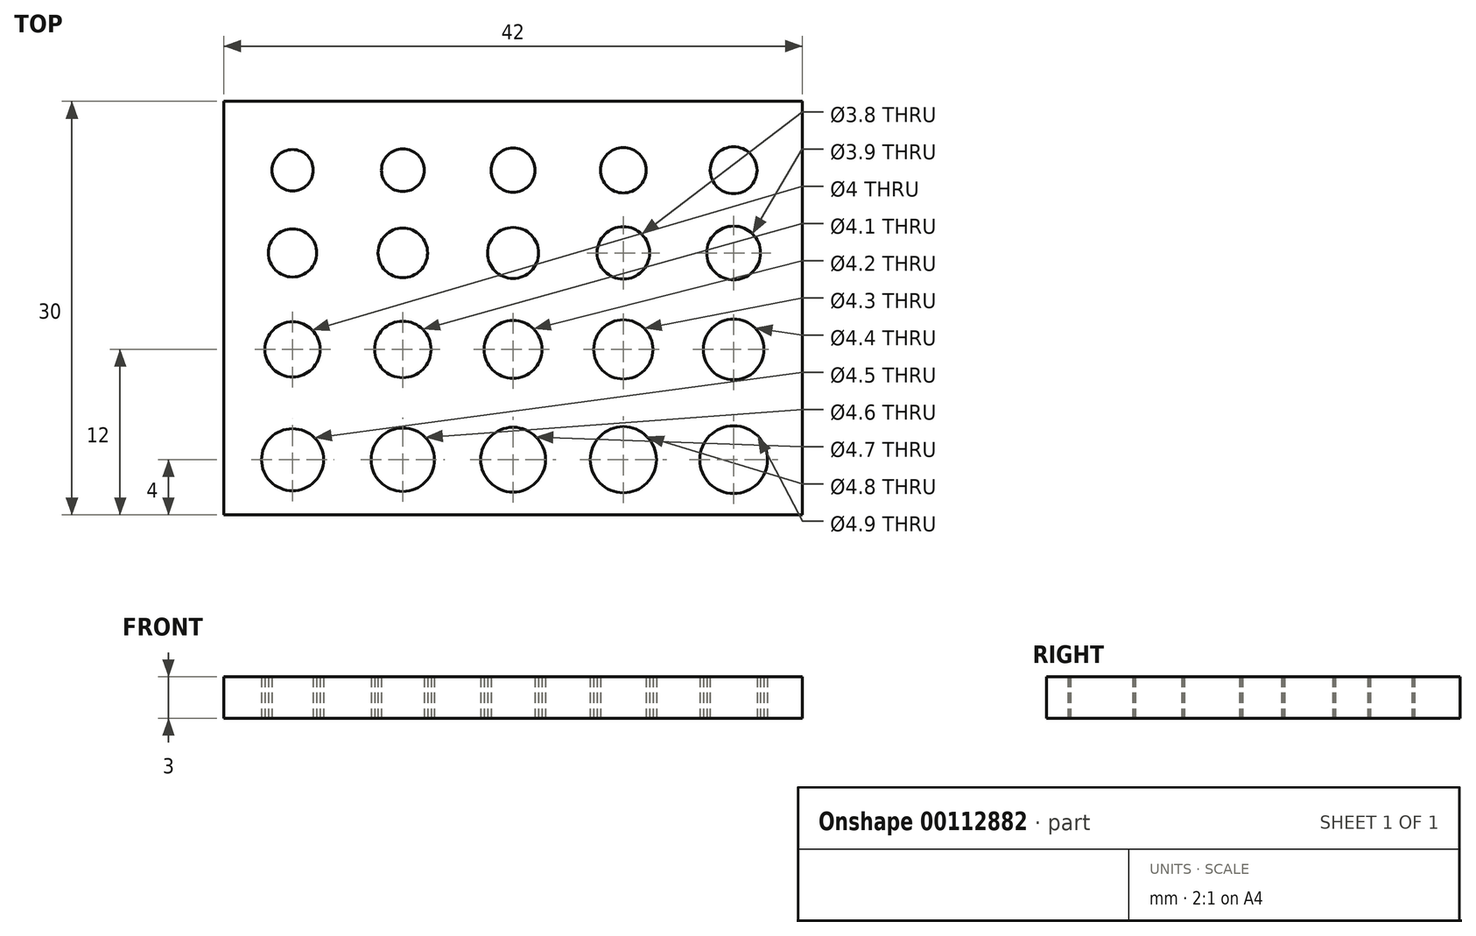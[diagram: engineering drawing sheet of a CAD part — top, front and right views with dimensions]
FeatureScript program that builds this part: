
annotation { "Feature Type Name" : "Feature", "Feature Type Description" : "" }
export const myFeature = defineFeature(function(context is Context, id is Id, definition is map)
    precondition{}
    {
        {
            var Q0;
            Q0=qCreatedBy(makeId("Top.planeOp"),FACE);
            var sketch = newSketch(context, id + "F0", { "sketchPlane" : qUnion([Q0])});
            skLineSegment(sketch, "E0.bottom", {"start": v(21, 15) * mm, "end": v(-21, 15) * mm});
            skLineSegment(sketch, "E0.top", {"start": v(21, -15) * mm, "end": v(-21, -15) * mm});
            skLineSegment(sketch, "E0.left", {"start": v(21, 15) * mm, "end": v(21, -15) * mm});
            skLineSegment(sketch, "E0.right", {"start": v(-21, 15) * mm, "end": v(-21, -15) * mm});
            skPoint(sketch, "E0.middle", {"position": v(0, 0) * mm});
            skPoint(sketch, "E1", {"position": v(-16, 10) * mm});
            skPoint(sketch, "E2.1.0.0", {"position": v(-8, 10) * mm});
            skPoint(sketch, "E2.2.0.0", {"position": v(0, 10) * mm});
            skLineSegment(sketch, "E2.direction1", {"start": v(-16, 10) * mm, "end": v(-8, 10) * mm, "construction": true});
            skPoint(sketch, "E3.0.3.0", {"position": v(8, 10) * mm});
            skPoint(sketch, "E3.0.4.0", {"position": v(16, 10) * mm});
            skPoint(sketch, "E4", {"position": v(-16, 4) * mm});
            skPoint(sketch, "E5", {"position": v(-16, -3) * mm});
            skPoint(sketch, "E6", {"position": v(-16, -11) * mm});
            skPoint(sketch, "E7.1.0.0", {"position": v(-8, 4) * mm});
            skPoint(sketch, "E7.2.0.0", {"position": v(0, 4) * mm});
            skLineSegment(sketch, "E7.direction1", {"start": v(-16, 4) * mm, "end": v(-8, 4) * mm, "construction": true});
            skPoint(sketch, "E8.0.3.0", {"position": v(8, 4) * mm});
            skPoint(sketch, "E8.0.4.0", {"position": v(16, 4) * mm});
            skPoint(sketch, "E9.1.0.0", {"position": v(-8, -3) * mm});
            skPoint(sketch, "E9.2.0.0", {"position": v(0, -3) * mm});
            skLineSegment(sketch, "E9.direction1", {"start": v(-16, -3) * mm, "end": v(-8, -3) * mm, "construction": true});
            skPoint(sketch, "E10.0.3.0", {"position": v(8, -3) * mm});
            skPoint(sketch, "E10.0.4.0", {"position": v(16, -3) * mm});
            skPoint(sketch, "E11.1.0.0", {"position": v(-8, -11) * mm});
            skPoint(sketch, "E11.2.0.0", {"position": v(0, -11) * mm});
            skLineSegment(sketch, "E11.direction1", {"start": v(-16, -11) * mm, "end": v(-8, -11) * mm, "construction": true});
            skPoint(sketch, "E12.0.3.0", {"position": v(8, -11) * mm});
            skPoint(sketch, "E12.0.4.0", {"position": v(16, -11) * mm});
            skSolve(sketch);
        }
        {
            var Q0;
            Q0=makeQuery(id+"F0.imprint","IMPRINT",FACE,{"disambiguationData":[TD([[makeQuery(id+"F0.imprint","IMPRINT",EDGE,{"derivedFrom":sQuery(id+"F0.wireOp",EDGE,"E0.bottom")}),1.0]])]});
            extrude(context, id + "F1", {"entities" : qUnion([Q0]), "depth" : 3 * mm});
        }
        {
            var Q0;
            Q0=sQuery(id+"F0.wireOp",VERTEX,"E1");
            var Q1;
            Q1=makeQuery(id+"F1.opExtrude","SWEPT_BODY",BODY,{"disambiguationData":[OSD([sQuery(id+"F0.wireOp",EDGE,"E0.bottom"),sQuery(id+"F0.wireOp",EDGE,"E0.top"),sQuery(id+"F0.wireOp",EDGE,"E0.left"),sQuery(id+"F0.wireOp",EDGE,"E0.right")])]});
            hole(context, id + "F2", {"style" : HoleStyle.SIMPLE, "endStyle" : HoleEndStyle.THROUGH, "oppositeDirection" : true, "holeDiameter" : 3 * mm, "startFromSketch" : true, "locations" : qUnion([Q0]), "scope" : qUnion([Q1]), "isTappedThrough" : true});
        }
        {
            var Q0;
            Q0=sQuery(id+"F0.wireOp",VERTEX,"E2.1.0.0");
            var Q1;
            Q1=makeQuery(id+"F1.opExtrude","SWEPT_BODY",BODY,{"disambiguationData":[OSD([sQuery(id+"F0.wireOp",EDGE,"E0.bottom"),sQuery(id+"F0.wireOp",EDGE,"E0.top"),sQuery(id+"F0.wireOp",EDGE,"E0.left"),sQuery(id+"F0.wireOp",EDGE,"E0.right")])]});
            hole(context, id + "F3", {"style" : HoleStyle.SIMPLE, "endStyle" : HoleEndStyle.THROUGH, "oppositeDirection" : true, "holeDiameter" : 3.1 * mm, "startFromSketch" : true, "locations" : qUnion([Q0]), "scope" : qUnion([Q1]), "isTappedThrough" : true});
        }
        {
            var Q0;
            Q0=sQuery(id+"F0.wireOp",VERTEX,"E2.2.0.0");
            var Q1;
            Q1=makeQuery(id+"F1.opExtrude","SWEPT_BODY",BODY,{"disambiguationData":[OSD([sQuery(id+"F0.wireOp",EDGE,"E0.bottom"),sQuery(id+"F0.wireOp",EDGE,"E0.top"),sQuery(id+"F0.wireOp",EDGE,"E0.left"),sQuery(id+"F0.wireOp",EDGE,"E0.right")])]});
            hole(context, id + "F4", {"style" : HoleStyle.SIMPLE, "endStyle" : HoleEndStyle.THROUGH, "oppositeDirection" : true, "holeDiameter" : 3.2 * mm, "startFromSketch" : true, "locations" : qUnion([Q0]), "scope" : qUnion([Q1]), "isTappedThrough" : true});
        }
        {
            var Q0;
            Q0=sQuery(id+"F0.wireOp",VERTEX,"E3.0.3.0");
            var Q1;
            Q1=makeQuery(id+"F1.opExtrude","SWEPT_BODY",BODY,{"disambiguationData":[OSD([sQuery(id+"F0.wireOp",EDGE,"E0.bottom"),sQuery(id+"F0.wireOp",EDGE,"E0.top"),sQuery(id+"F0.wireOp",EDGE,"E0.left"),sQuery(id+"F0.wireOp",EDGE,"E0.right")])]});
            hole(context, id + "F5", {"style" : HoleStyle.SIMPLE, "endStyle" : HoleEndStyle.THROUGH, "oppositeDirection" : true, "holeDiameter" : 3.3 * mm, "startFromSketch" : true, "locations" : qUnion([Q0]), "scope" : qUnion([Q1]), "isTappedThrough" : true});
        }
        {
            var Q0;
            Q0=sQuery(id+"F0.wireOp",VERTEX,"E3.0.4.0");
            var Q1;
            Q1=makeQuery(id+"F1.opExtrude","SWEPT_BODY",BODY,{"disambiguationData":[OSD([sQuery(id+"F0.wireOp",EDGE,"E0.bottom"),sQuery(id+"F0.wireOp",EDGE,"E0.top"),sQuery(id+"F0.wireOp",EDGE,"E0.left"),sQuery(id+"F0.wireOp",EDGE,"E0.right")])]});
            hole(context, id + "F6", {"style" : HoleStyle.SIMPLE, "endStyle" : HoleEndStyle.THROUGH, "oppositeDirection" : true, "holeDiameter" : 3.4 * mm, "startFromSketch" : true, "locations" : qUnion([Q0]), "scope" : qUnion([Q1]), "isTappedThrough" : true});
        }
        {
            var Q0;
            Q0=sQuery(id+"F0.wireOp",VERTEX,"E4");
            var Q1;
            Q1=makeQuery(id+"F1.opExtrude","SWEPT_BODY",BODY,{"disambiguationData":[OSD([sQuery(id+"F0.wireOp",EDGE,"E0.bottom"),sQuery(id+"F0.wireOp",EDGE,"E0.top"),sQuery(id+"F0.wireOp",EDGE,"E0.left"),sQuery(id+"F0.wireOp",EDGE,"E0.right")])]});
            hole(context, id + "F7", {"style" : HoleStyle.SIMPLE, "endStyle" : HoleEndStyle.THROUGH, "oppositeDirection" : true, "holeDiameter" : 3.5 * mm, "startFromSketch" : true, "locations" : qUnion([Q0]), "scope" : qUnion([Q1]), "isTappedThrough" : true});
        }
        {
            var Q0;
            Q0=sQuery(id+"F0.wireOp",VERTEX,"E7.1.0.0");
            var Q1;
            Q1=makeQuery(id+"F1.opExtrude","SWEPT_BODY",BODY,{"disambiguationData":[OSD([sQuery(id+"F0.wireOp",EDGE,"E0.bottom"),sQuery(id+"F0.wireOp",EDGE,"E0.top"),sQuery(id+"F0.wireOp",EDGE,"E0.left"),sQuery(id+"F0.wireOp",EDGE,"E0.right")])]});
            hole(context, id + "F8", {"style" : HoleStyle.SIMPLE, "endStyle" : HoleEndStyle.THROUGH, "oppositeDirection" : true, "holeDiameter" : 3.6 * mm, "startFromSketch" : true, "locations" : qUnion([Q0]), "scope" : qUnion([Q1]), "isTappedThrough" : true});
        }
        {
            var Q0;
            Q0=sQuery(id+"F0.wireOp",VERTEX,"E7.2.0.0");
            var Q1;
            Q1=makeQuery(id+"F1.opExtrude","SWEPT_BODY",BODY,{"disambiguationData":[OSD([sQuery(id+"F0.wireOp",EDGE,"E0.bottom"),sQuery(id+"F0.wireOp",EDGE,"E0.top"),sQuery(id+"F0.wireOp",EDGE,"E0.left"),sQuery(id+"F0.wireOp",EDGE,"E0.right")])]});
            hole(context, id + "F9", {"style" : HoleStyle.SIMPLE, "endStyle" : HoleEndStyle.THROUGH, "oppositeDirection" : true, "holeDiameter" : 3.7 * mm, "startFromSketch" : true, "locations" : qUnion([Q0]), "scope" : qUnion([Q1]), "isTappedThrough" : true});
        }
        {
            var Q0;
            Q0=sQuery(id+"F0.wireOp",VERTEX,"E8.0.3.0");
            var Q1;
            Q1=makeQuery(id+"F1.opExtrude","SWEPT_BODY",BODY,{"disambiguationData":[OSD([sQuery(id+"F0.wireOp",EDGE,"E0.bottom"),sQuery(id+"F0.wireOp",EDGE,"E0.top"),sQuery(id+"F0.wireOp",EDGE,"E0.left"),sQuery(id+"F0.wireOp",EDGE,"E0.right")])]});
            hole(context, id + "F10", {"style" : HoleStyle.SIMPLE, "endStyle" : HoleEndStyle.THROUGH, "oppositeDirection" : true, "holeDiameter" : 3.8 * mm, "startFromSketch" : true, "locations" : qUnion([Q0]), "scope" : qUnion([Q1]), "isTappedThrough" : true});
        }
        {
            var Q0;
            Q0=sQuery(id+"F0.wireOp",VERTEX,"E8.0.4.0");
            var Q1;
            Q1=makeQuery(id+"F1.opExtrude","SWEPT_BODY",BODY,{"disambiguationData":[OSD([sQuery(id+"F0.wireOp",EDGE,"E0.bottom"),sQuery(id+"F0.wireOp",EDGE,"E0.top"),sQuery(id+"F0.wireOp",EDGE,"E0.left"),sQuery(id+"F0.wireOp",EDGE,"E0.right")])]});
            hole(context, id + "F11", {"style" : HoleStyle.SIMPLE, "endStyle" : HoleEndStyle.THROUGH, "oppositeDirection" : true, "holeDiameter" : 3.9 * mm, "startFromSketch" : true, "locations" : qUnion([Q0]), "scope" : qUnion([Q1]), "isTappedThrough" : true});
        }
        {
            var Q0;
            Q0=sQuery(id+"F0.wireOp",VERTEX,"E5");
            var Q1;
            Q1=makeQuery(id+"F1.opExtrude","SWEPT_BODY",BODY,{"disambiguationData":[OSD([sQuery(id+"F0.wireOp",EDGE,"E0.bottom"),sQuery(id+"F0.wireOp",EDGE,"E0.top"),sQuery(id+"F0.wireOp",EDGE,"E0.left"),sQuery(id+"F0.wireOp",EDGE,"E0.right")])]});
            hole(context, id + "F12", {"style" : HoleStyle.SIMPLE, "endStyle" : HoleEndStyle.THROUGH, "oppositeDirection" : true, "holeDiameter" : 4 * mm, "startFromSketch" : true, "locations" : qUnion([Q0]), "scope" : qUnion([Q1]), "isTappedThrough" : true});
        }
        {
            var Q0;
            Q0=sQuery(id+"F0.wireOp",VERTEX,"E9.1.0.0");
            var Q1;
            Q1=makeQuery(id+"F1.opExtrude","SWEPT_BODY",BODY,{"disambiguationData":[OSD([sQuery(id+"F0.wireOp",EDGE,"E0.bottom"),sQuery(id+"F0.wireOp",EDGE,"E0.top"),sQuery(id+"F0.wireOp",EDGE,"E0.left"),sQuery(id+"F0.wireOp",EDGE,"E0.right")])]});
            hole(context, id + "F13", {"style" : HoleStyle.SIMPLE, "endStyle" : HoleEndStyle.THROUGH, "oppositeDirection" : true, "holeDiameter" : 4.1 * mm, "startFromSketch" : true, "locations" : qUnion([Q0]), "scope" : qUnion([Q1]), "isTappedThrough" : true});
        }
        {
            var Q0;
            Q0=sQuery(id+"F0.wireOp",VERTEX,"E9.2.0.0");
            var Q1;
            Q1=makeQuery(id+"F1.opExtrude","SWEPT_BODY",BODY,{"disambiguationData":[OSD([sQuery(id+"F0.wireOp",EDGE,"E0.bottom"),sQuery(id+"F0.wireOp",EDGE,"E0.top"),sQuery(id+"F0.wireOp",EDGE,"E0.left"),sQuery(id+"F0.wireOp",EDGE,"E0.right")])]});
            hole(context, id + "F14", {"style" : HoleStyle.SIMPLE, "endStyle" : HoleEndStyle.THROUGH, "oppositeDirection" : true, "holeDiameter" : 4.2 * mm, "startFromSketch" : true, "locations" : qUnion([Q0]), "scope" : qUnion([Q1]), "isTappedThrough" : true});
        }
        {
            var Q0;
            Q0=sQuery(id+"F0.wireOp",VERTEX,"E10.0.3.0");
            var Q1;
            Q1=makeQuery(id+"F1.opExtrude","SWEPT_BODY",BODY,{"disambiguationData":[OSD([sQuery(id+"F0.wireOp",EDGE,"E0.bottom"),sQuery(id+"F0.wireOp",EDGE,"E0.top"),sQuery(id+"F0.wireOp",EDGE,"E0.left"),sQuery(id+"F0.wireOp",EDGE,"E0.right")])]});
            hole(context, id + "F15", {"style" : HoleStyle.SIMPLE, "endStyle" : HoleEndStyle.THROUGH, "oppositeDirection" : true, "holeDiameter" : 4.3 * mm, "startFromSketch" : true, "locations" : qUnion([Q0]), "scope" : qUnion([Q1]), "isTappedThrough" : true});
        }
        {
            var Q0;
            Q0=sQuery(id+"F0.wireOp",VERTEX,"E10.0.4.0");
            var Q1;
            Q1=makeQuery(id+"F1.opExtrude","SWEPT_BODY",BODY,{"disambiguationData":[OSD([sQuery(id+"F0.wireOp",EDGE,"E0.bottom"),sQuery(id+"F0.wireOp",EDGE,"E0.top"),sQuery(id+"F0.wireOp",EDGE,"E0.left"),sQuery(id+"F0.wireOp",EDGE,"E0.right")])]});
            hole(context, id + "F16", {"style" : HoleStyle.SIMPLE, "endStyle" : HoleEndStyle.THROUGH, "oppositeDirection" : true, "holeDiameter" : 4.4 * mm, "startFromSketch" : true, "locations" : qUnion([Q0]), "scope" : qUnion([Q1]), "isTappedThrough" : true});
        }
        {
            var Q0;
            Q0=sQuery(id+"F0.wireOp",VERTEX,"E6");
            var Q1;
            Q1=makeQuery(id+"F1.opExtrude","SWEPT_BODY",BODY,{"disambiguationData":[OSD([sQuery(id+"F0.wireOp",EDGE,"E0.bottom"),sQuery(id+"F0.wireOp",EDGE,"E0.top"),sQuery(id+"F0.wireOp",EDGE,"E0.left"),sQuery(id+"F0.wireOp",EDGE,"E0.right")])]});
            hole(context, id + "F17", {"style" : HoleStyle.SIMPLE, "endStyle" : HoleEndStyle.THROUGH, "oppositeDirection" : true, "holeDiameter" : 4.5 * mm, "startFromSketch" : true, "locations" : qUnion([Q0]), "scope" : qUnion([Q1]), "isTappedThrough" : true});
        }
        {
            var Q0;
            Q0=sQuery(id+"F0.wireOp",VERTEX,"E11.1.0.0");
            var Q1;
            Q1=makeQuery(id+"F1.opExtrude","SWEPT_BODY",BODY,{"disambiguationData":[OSD([sQuery(id+"F0.wireOp",EDGE,"E0.bottom"),sQuery(id+"F0.wireOp",EDGE,"E0.top"),sQuery(id+"F0.wireOp",EDGE,"E0.left"),sQuery(id+"F0.wireOp",EDGE,"E0.right")])]});
            hole(context, id + "F18", {"style" : HoleStyle.SIMPLE, "endStyle" : HoleEndStyle.THROUGH, "oppositeDirection" : true, "holeDiameter" : 4.6 * mm, "startFromSketch" : true, "locations" : qUnion([Q0]), "scope" : qUnion([Q1]), "isTappedThrough" : true});
        }
        {
            var Q0;
            Q0=sQuery(id+"F0.wireOp",VERTEX,"E11.2.0.0");
            var Q1;
            Q1=makeQuery(id+"F1.opExtrude","SWEPT_BODY",BODY,{"disambiguationData":[OSD([sQuery(id+"F0.wireOp",EDGE,"E0.bottom"),sQuery(id+"F0.wireOp",EDGE,"E0.top"),sQuery(id+"F0.wireOp",EDGE,"E0.left"),sQuery(id+"F0.wireOp",EDGE,"E0.right")])]});
            hole(context, id + "F19", {"style" : HoleStyle.SIMPLE, "endStyle" : HoleEndStyle.THROUGH, "oppositeDirection" : true, "holeDiameter" : 4.7 * mm, "startFromSketch" : true, "locations" : qUnion([Q0]), "scope" : qUnion([Q1]), "isTappedThrough" : true});
        }
        {
            var Q0;
            Q0=sQuery(id+"F0.wireOp",VERTEX,"E12.0.3.0");
            var Q1;
            Q1=makeQuery(id+"F1.opExtrude","SWEPT_BODY",BODY,{"disambiguationData":[OSD([sQuery(id+"F0.wireOp",EDGE,"E0.bottom"),sQuery(id+"F0.wireOp",EDGE,"E0.top"),sQuery(id+"F0.wireOp",EDGE,"E0.left"),sQuery(id+"F0.wireOp",EDGE,"E0.right")])]});
            hole(context, id + "F20", {"style" : HoleStyle.SIMPLE, "endStyle" : HoleEndStyle.THROUGH, "oppositeDirection" : true, "holeDiameter" : 4.8 * mm, "startFromSketch" : true, "locations" : qUnion([Q0]), "scope" : qUnion([Q1]), "isTappedThrough" : true});
        }
        {
            var Q0;
            Q0=sQuery(id+"F0.wireOp",VERTEX,"E12.0.4.0");
            var Q1;
            Q1=makeQuery(id+"F1.opExtrude","SWEPT_BODY",BODY,{"disambiguationData":[OSD([sQuery(id+"F0.wireOp",EDGE,"E0.bottom"),sQuery(id+"F0.wireOp",EDGE,"E0.top"),sQuery(id+"F0.wireOp",EDGE,"E0.left"),sQuery(id+"F0.wireOp",EDGE,"E0.right")])]});
            hole(context, id + "F21", {"style" : HoleStyle.SIMPLE, "endStyle" : HoleEndStyle.THROUGH, "oppositeDirection" : true, "holeDiameter" : 4.9 * mm, "startFromSketch" : true, "locations" : qUnion([Q0]), "scope" : qUnion([Q1]), "isTappedThrough" : true});
        }
    });
